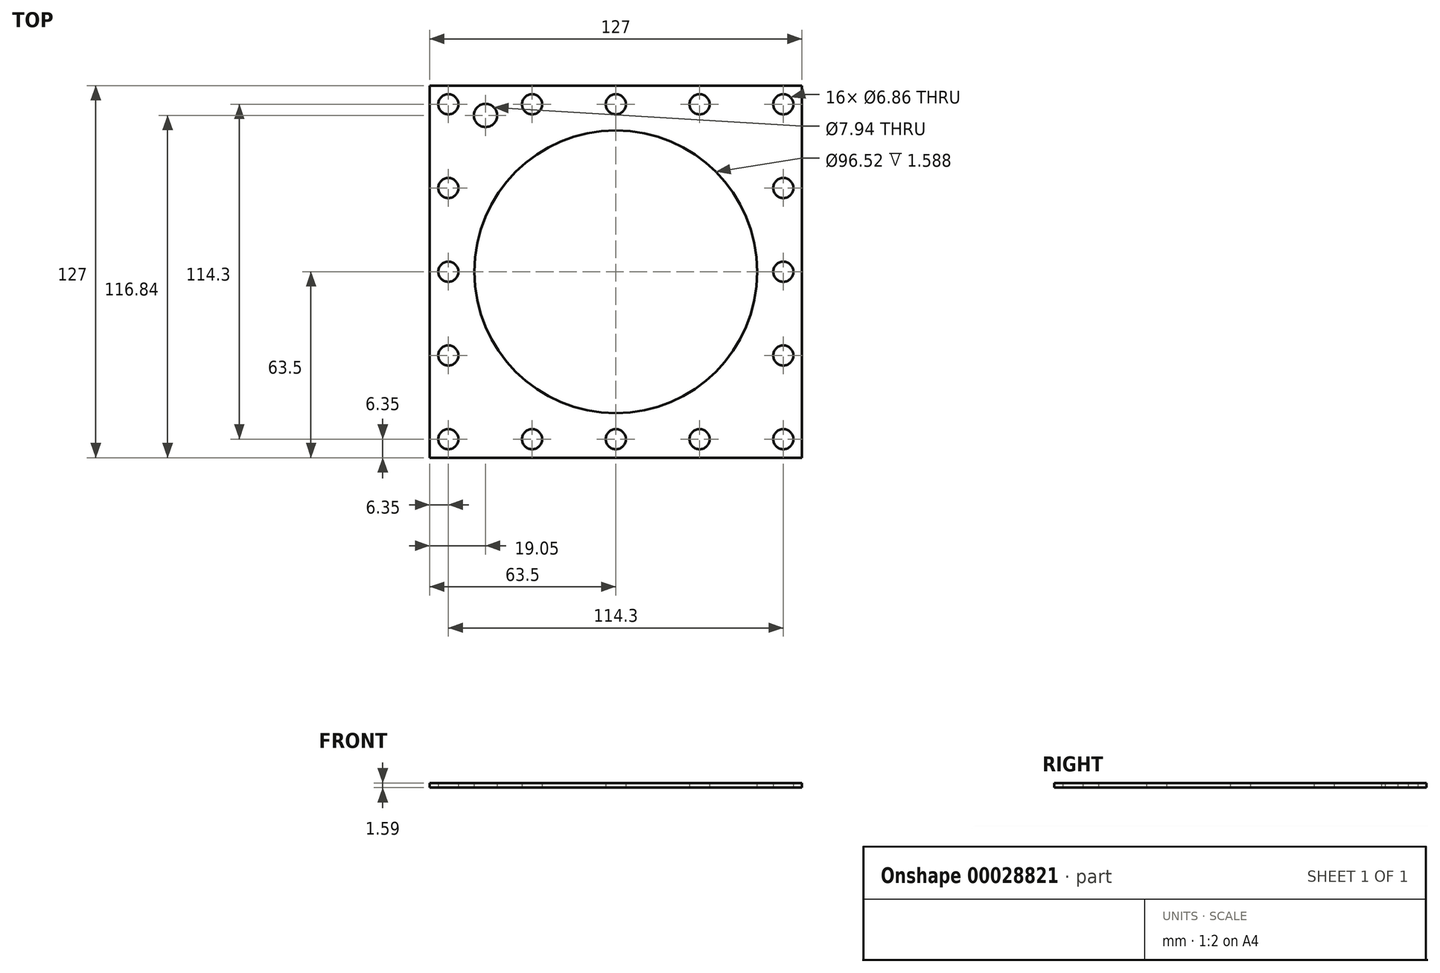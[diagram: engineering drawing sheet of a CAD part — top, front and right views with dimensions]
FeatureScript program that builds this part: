
annotation { "Feature Type Name" : "Feature", "Feature Type Description" : "" }
export const myFeature = defineFeature(function(context is Context, id is Id, definition is map)
    precondition{}
    {
        {
            var Q0;
            Q0=qCreatedBy(makeId("Top.planeOp"),FACE);
            var sketch = newSketch(context, id + "F0", { "sketchPlane" : qUnion([Q0])});
            skLineSegment(sketch, "E0.rect.bottom", {"start": v(63.5, 63.5) * mm, "end": v(-63.5, 63.5) * mm});
            skLineSegment(sketch, "E0.rect.top", {"start": v(63.5, -63.5) * mm, "end": v(-63.5, -63.5) * mm});
            skLineSegment(sketch, "E0.rect.left", {"start": v(63.5, 63.5) * mm, "end": v(63.5, -63.5) * mm});
            skLineSegment(sketch, "E0.rect.right", {"start": v(-63.5, 63.5) * mm, "end": v(-63.5, -63.5) * mm});
            skPoint(sketch, "E0.rect.middle", {"position": v(0, 0) * mm});
            skCircle(sketch, "E1", {"center": v(-44.45, 53.34) * mm, "radius": 3.97 * mm});
            skCircle(sketch, "E2", {"center": v(0, 0) * mm, "radius": 47.56 * mm, "construction": true});
            skLineSegment(sketch, "E3.rect.bottom", {"start": v(-57.15, 57.15) * mm, "end": v(57.15, 57.15) * mm, "construction": true});
            skLineSegment(sketch, "E3.rect.top", {"start": v(-57.15, -57.15) * mm, "end": v(57.15, -57.15) * mm, "construction": true});
            skLineSegment(sketch, "E3.rect.left", {"start": v(-57.15, 57.15) * mm, "end": v(-57.15, -57.15) * mm, "construction": true});
            skLineSegment(sketch, "E3.rect.right", {"start": v(57.15, 57.15) * mm, "end": v(57.15, -57.15) * mm, "construction": true});
            skPoint(sketch, "E4", {"position": v(0, 57.15) * mm});
            skPoint(sketch, "E5", {"position": v(57.15, 0) * mm});
            skPoint(sketch, "E6", {"position": v(0, -57.15) * mm});
            skPoint(sketch, "E7", {"position": v(-57.15, 0) * mm});
            skCircle(sketch, "E8", {"center": v(-57.15, 57.15) * mm, "radius": 3.43 * mm});
            skCircle(sketch, "E9", {"center": v(0, 57.15) * mm, "radius": 3.43 * mm});
            skCircle(sketch, "E10", {"center": v(57.15, 57.15) * mm, "radius": 3.43 * mm});
            skCircle(sketch, "E11", {"center": v(57.15, 0) * mm, "radius": 3.43 * mm});
            skCircle(sketch, "E12", {"center": v(57.15, -57.15) * mm, "radius": 3.43 * mm});
            skCircle(sketch, "E13", {"center": v(0, -57.15) * mm, "radius": 3.43 * mm});
            skCircle(sketch, "E14", {"center": v(-57.15, -57.15) * mm, "radius": 3.43 * mm});
            skCircle(sketch, "E15", {"center": v(-57.15, 0) * mm, "radius": 3.43 * mm});
            skLineSegment(sketch, "E16.rect.bottom", {"start": v(-50, 50) * mm, "end": v(50, 50) * mm, "construction": true});
            skLineSegment(sketch, "E16.rect.top", {"start": v(-50, -50) * mm, "end": v(50, -50) * mm, "construction": true});
            skLineSegment(sketch, "E16.rect.left", {"start": v(-50, 50) * mm, "end": v(-50, -50) * mm, "construction": true});
            skLineSegment(sketch, "E16.rect.right", {"start": v(50, 50) * mm, "end": v(50, -50) * mm, "construction": true});
            skCircle(sketch, "E17", {"center": v(28.57, 57.15) * mm, "radius": 3.43 * mm});
            skCircle(sketch, "E18", {"center": v(57.15, 28.58) * mm, "radius": 3.43 * mm});
            skCircle(sketch, "E19", {"center": v(57.15, -28.58) * mm, "radius": 3.43 * mm});
            skCircle(sketch, "E20", {"center": v(28.58, -57.15) * mm, "radius": 3.43 * mm});
            skCircle(sketch, "E21", {"center": v(-28.58, -57.15) * mm, "radius": 3.43 * mm});
            skCircle(sketch, "E22", {"center": v(-57.15, -28.58) * mm, "radius": 3.43 * mm});
            skCircle(sketch, "E23", {"center": v(-57.15, 28.58) * mm, "radius": 3.43 * mm});
            skCircle(sketch, "E24", {"center": v(-28.58, 57.15) * mm, "radius": 3.43 * mm});
            skSolve(sketch);
        }
        {
            var Q0;
            Q0=qSketchRegion(id+"F0",true);
            var Q1;
            {var subQ21=sQuery(id+"F0.wireOp",EDGE,"f6949425-b88c-4a0e-8302-07c829dae053.0");var subQ27=sQuery(id+"F0.wireOp",EDGE,"5bd9be1d-ee3e-4944-9718-c5885c81100e");var subQ29=makeQuery(id+"F0.imprint","INTERSECT",VERTEX,{"derivedFrom":[subQ21,subQ27]});Q1=makeQuery(id+"F0.imprint","IMPRINT",FACE,{"disambiguationData":[TD([[makeQuery(id+"F0.imprint","IMPRINT",EDGE,{"disambiguationData":[TD([[subQ29,-1.0]])],"derivedFrom":subQ21}),-1.0]])]});}
            extrude(context, id + "F1", {"entities" : qUnion([Q0, Q1]), "depth" : 1.59 * mm});
        }
        {
            var Q0;
            Q0=makeQuery(id+"F1.opExtrude","CAP_FACE",FACE,{"disambiguationData":[OSD([sQuery(id+"F0.wireOp",EDGE,"E0.rect.bottom"),sQuery(id+"F0.wireOp",EDGE,"E0.rect.top"),sQuery(id+"F0.wireOp",EDGE,"E0.rect.left"),sQuery(id+"F0.wireOp",EDGE,"E0.rect.right"),sQuery(id+"F0.wireOp",EDGE,"1b772a9f-1761-4584-9b2b-9508be88e127"),sQuery(id+"F0.wireOp",EDGE,"5bd9be1d-ee3e-4944-9718-c5885c81100e"),sQuery(id+"F0.wireOp",EDGE,"a4b3396b-acb1-4126-9ecc-f22d3d9e1673"),sQuery(id+"F0.wireOp",EDGE,"6f9071d3-dfce-459a-96f3-6cfad81b1998"),sQuery(id+"F0.wireOp",EDGE,"8e253895-448c-4740-8d73-7ad6095a0958"),sQuery(id+"F0.wireOp",EDGE,"49ddc21f-956a-45ed-accb-e36c5fb570fd"),sQuery(id+"F0.wireOp",EDGE,"4c855955-bd80-4a33-8133-648448e085db"),sQuery(id+"F0.wireOp",EDGE,"5388e59b-5754-40e4-abb9-c8fe2573278b"),sQuery(id+"F0.wireOp",EDGE,"cb97a597-6742-4d9a-a243-e93a22987a54"),sQuery(id+"F0.wireOp",EDGE,"2f3ac294-263d-4671-b671-df59b6b99c8d")])],"isStart":false});
            var sketch = newSketch(context, id + "F2", { "sketchPlane" : qUnion([Q0])});
            skCircle(sketch, "E25", {"center": v(0, 0) * mm, "radius": 48.26 * mm});
            skSolve(sketch);
        }
        {
            var Q0;
            Q0=qSketchRegion(id+"F2",true);
            extrude(context, id + "F3", {"entities" : qUnion([Q0]), "operationType" : NewBodyOperationType.REMOVE, "endBound" : BoundingType.THROUGH_ALL, "oppositeDirection" : true, "depth" : 3.17 * mm});
        }
    });
